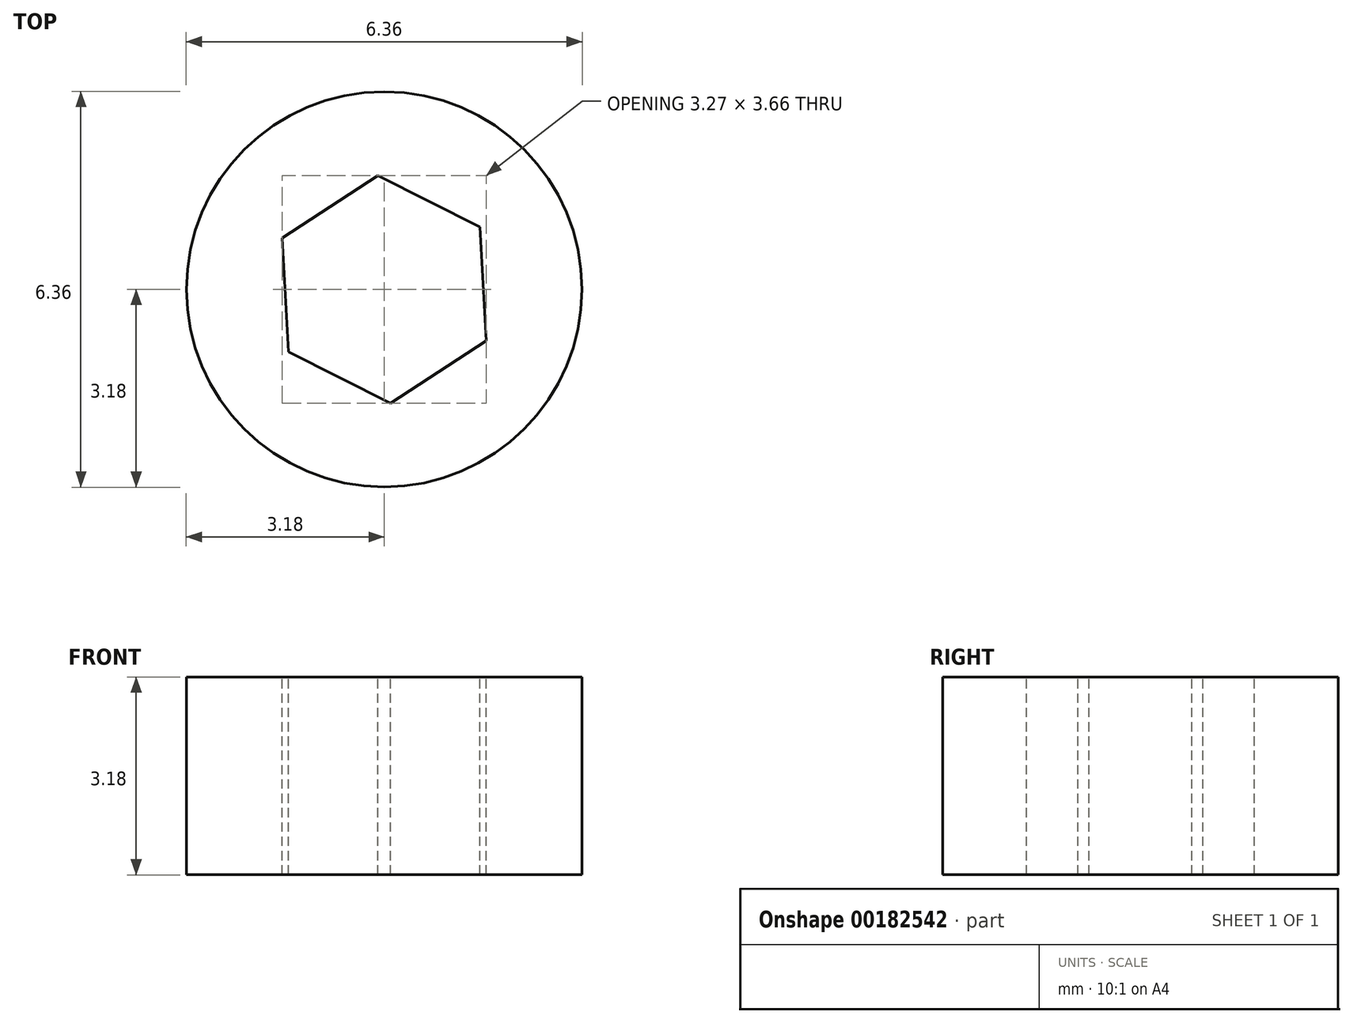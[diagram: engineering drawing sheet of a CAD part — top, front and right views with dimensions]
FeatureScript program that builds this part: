
annotation { "Feature Type Name" : "Feature", "Feature Type Description" : "" }
export const myFeature = defineFeature(function(context is Context, id is Id, definition is map)
    precondition{}
    {
        {
            var Q0;
            Q0=qCreatedBy(makeId("Top.planeOp"),FACE);
            var sketch = newSketch(context, id + "F0", { "sketchPlane" : qUnion([Q0])});
            skCircle(sketch, "E0", {"center": v(0, 0) * mm, "radius": 3.18 * mm});
            skCircle(sketch, "E1.cCircle", {"center": v(0, 0) * mm, "radius": 1.59 * mm, "construction": true});
            skLineSegment(sketch, "E1.0", {"start": v(-1.64, 0.83) * mm, "end": v(-0.1, 1.83) * mm});
            skLineSegment(sketch, "E1.1", {"start": v(-0.1, 1.83) * mm, "end": v(1.53, 1) * mm});
            skLineSegment(sketch, "E1.2", {"start": v(1.53, 1) * mm, "end": v(1.64, -0.83) * mm});
            skLineSegment(sketch, "E1.3", {"start": v(1.64, -0.83) * mm, "end": v(0.1, -1.83) * mm});
            skLineSegment(sketch, "E1.4", {"start": v(0.1, -1.83) * mm, "end": v(-1.53, -1) * mm});
            skLineSegment(sketch, "E1.5", {"start": v(-1.53, -1) * mm, "end": v(-1.64, 0.83) * mm});
            skPoint(sketch, "E1.0.midPoint", {"position": v(-0.87, 1.33) * mm});
            skSolve(sketch);
        }
        {
            var Q0;
            Q0 = qSketchRegion(id + "F0", true);
            extrude(context, id + "F1", {"entities" : qUnion([Q0]), "oppositeDirection" : true, "depth" : 3.17 * mm});
        }
    });
